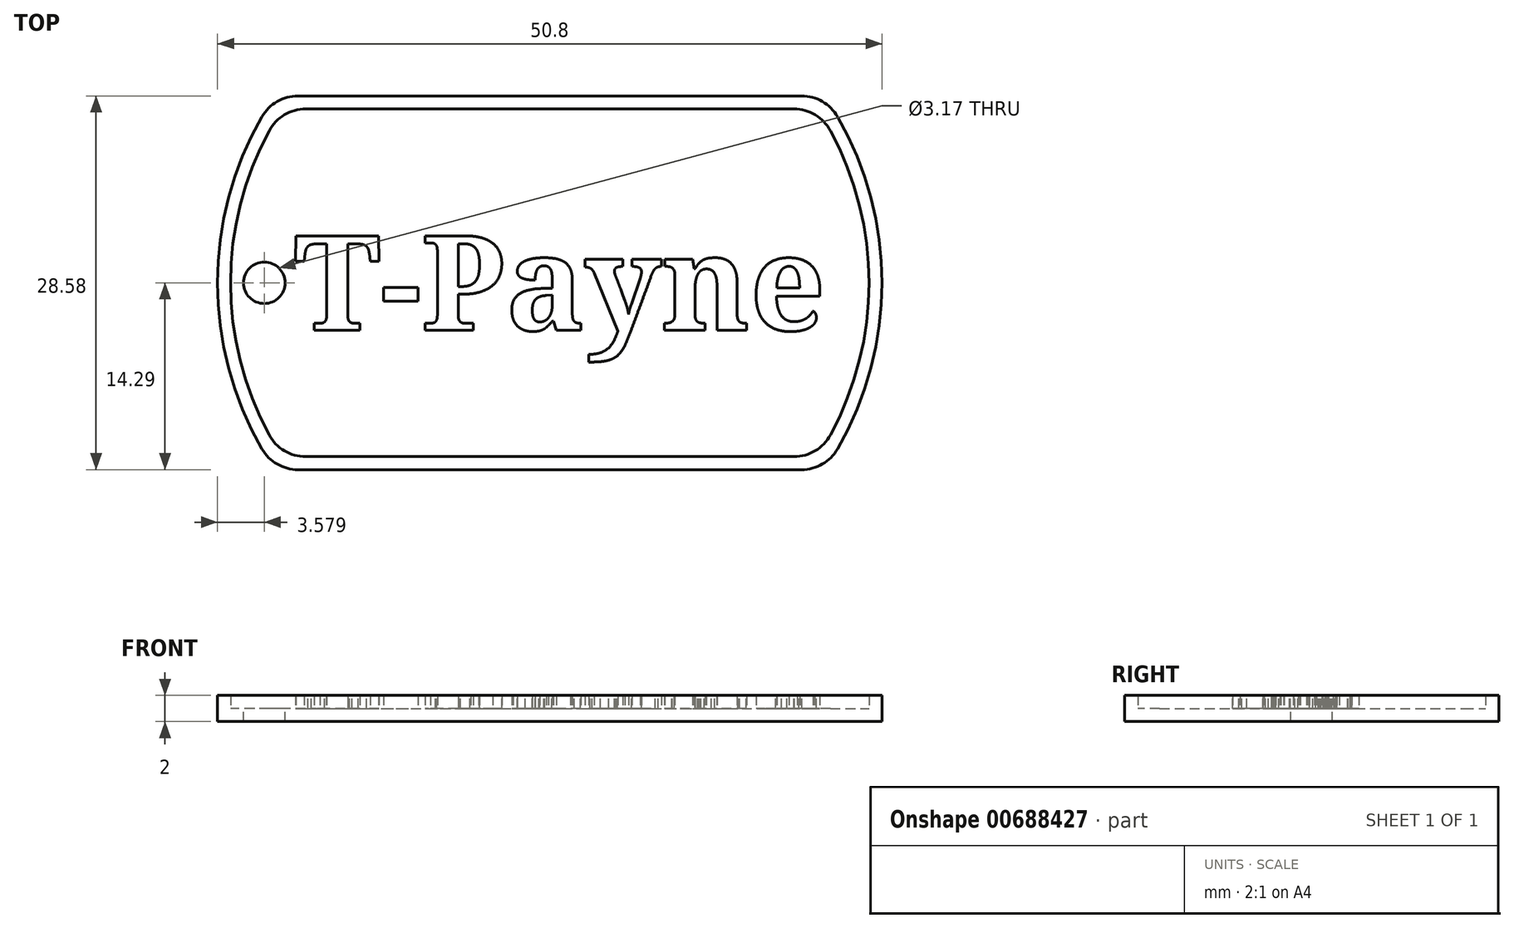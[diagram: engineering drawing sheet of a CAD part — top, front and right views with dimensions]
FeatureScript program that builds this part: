
annotation { "Feature Type Name" : "Feature", "Feature Type Description" : "" }
export const myFeature = defineFeature(function(context is Context, id is Id, definition is map)
    precondition{}
    {
        {
            var Q0;
            Q0=qCreatedBy(makeId("Top.planeOp"),FACE);
            var sketch = newSketch(context, id + "F0", { "sketchPlane" : qUnion([Q0])});
            skArc(sketch, "E0", {"start": v(-22, 12.7) * mm, "mid": v(-25.4, 0) * mm, "end": v(-22, -12.7) * mm});
            skLineSegment(sketch, "E1.top", {"start": v(-19.25, -14.29) * mm, "end": v(19.25, -14.29) * mm});
            skArc(sketch, "E2.trimOffspring", {"start": v(22, -12.7) * mm, "mid": v(25.4, 0) * mm, "end": v(22, 12.7) * mm});
            skLineSegment(sketch, "E3", {"start": v(-19.25, 14.29) * mm, "end": v(19.25, 14.29) * mm});
            skPoint(sketch, "E4.visualSharp", {"position": v(-21, 14.29) * mm});
            skArc(sketch, "E4.filletArc", {"start": v(-19.25, 14.29) * mm, "mid": v(-20.83, 13.86) * mm, "end": v(-22, 12.7) * mm});
            skPoint(sketch, "E5.visualSharp", {"position": v(21, 14.29) * mm});
            skArc(sketch, "E5.filletArc", {"start": v(22, 12.7) * mm, "mid": v(20.83, 13.86) * mm, "end": v(19.25, 14.29) * mm});
            skPoint(sketch, "E6.visualSharp", {"position": v(21, -14.29) * mm});
            skArc(sketch, "E6.filletArc", {"start": v(19.25, -14.29) * mm, "mid": v(20.83, -13.86) * mm, "end": v(22, -12.7) * mm});
            skPoint(sketch, "E7.visualSharp", {"position": v(-21, -14.29) * mm});
            skArc(sketch, "E7.filletArc", {"start": v(-22, -12.7) * mm, "mid": v(-20.83, -13.86) * mm, "end": v(-19.25, -14.29) * mm});
            skSolve(sketch);
        }
        {
            var Q0;
            Q0=makeQuery(id+"F0.imprint","IMPRINT",FACE,{"disambiguationData":[TD([[makeQuery(id+"F0.imprint","IMPRINT",EDGE,{"derivedFrom":sQuery(id+"F0.wireOp",EDGE,"E0")}),1.0]])]});
            extrude(context, id + "F1", {"entities" : qUnion([Q0]), "depth" : 1 * mm, "offsetDistance" : 25.4 * mm});
        }
        {
            var Q0;
            Q0=makeQuery(id+"F1.opExtrude","CAP_FACE",FACE,{"disambiguationData":[OSD([sQuery(id+"F0.wireOp",EDGE,"E0"),sQuery(id+"F0.wireOp",EDGE,"E1.top"),sQuery(id+"F0.wireOp",EDGE,"E2.trimOffspring"),sQuery(id+"F0.wireOp",EDGE,"E3"),sQuery(id+"F0.wireOp",EDGE,"E4.filletArc"),sQuery(id+"F0.wireOp",EDGE,"E5.filletArc"),sQuery(id+"F0.wireOp",EDGE,"E6.filletArc"),sQuery(id+"F0.wireOp",EDGE,"E7.filletArc")])],"isStart":false});
            var sketch = newSketch(context, id + "F2", { "sketchPlane" : qUnion([Q0])});
            skLineSegment(sketch, "E8.0", {"start": v(-18.66, 13.29) * mm, "end": v(18.66, 13.29) * mm});
            skArc(sketch, "E8.1", {"start": v(-21.45, 11.63) * mm, "mid": v(-24.4, 0) * mm, "end": v(-21.45, -11.63) * mm});
            skLineSegment(sketch, "E8.2", {"start": v(-18.66, -13.29) * mm, "end": v(18.66, -13.29) * mm});
            skArc(sketch, "E8.3", {"start": v(21.45, -11.63) * mm, "mid": v(24.4, 0) * mm, "end": v(21.45, 11.63) * mm});
            skPoint(sketch, "E9.visualSharp", {"position": v(-20.46, 13.29) * mm});
            skArc(sketch, "E9.filletArc", {"start": v(-18.66, 13.29) * mm, "mid": v(-20.29, 12.84) * mm, "end": v(-21.45, 11.63) * mm});
            skPoint(sketch, "E10.visualSharp", {"position": v(20.46, 13.29) * mm});
            skArc(sketch, "E10.filletArc", {"start": v(21.45, 11.63) * mm, "mid": v(20.29, 12.84) * mm, "end": v(18.66, 13.29) * mm});
            skPoint(sketch, "E11.visualSharp", {"position": v(20.46, -13.29) * mm});
            skArc(sketch, "E11.filletArc", {"start": v(18.66, -13.29) * mm, "mid": v(20.29, -12.84) * mm, "end": v(21.45, -11.63) * mm});
            skPoint(sketch, "E12.visualSharp", {"position": v(-20.46, -13.29) * mm});
            skArc(sketch, "E12.filletArc", {"start": v(-21.45, -11.63) * mm, "mid": v(-20.29, -12.84) * mm, "end": v(-18.66, -13.29) * mm});
            skLineSegment(sketch, "E13.0", {"start": v(-19.25, 14.29) * mm, "end": v(19.25, 14.29) * mm});
            skArc(sketch, "E13.1", {"start": v(-22, 12.7) * mm, "mid": v(-25.4, 0) * mm, "end": v(-22, -12.7) * mm});
            skLineSegment(sketch, "E13.2", {"start": v(-19.25, -14.29) * mm, "end": v(19.25, -14.29) * mm});
            skArc(sketch, "E13.3", {"start": v(22, -12.7) * mm, "mid": v(25.4, 0) * mm, "end": v(22, 12.7) * mm});
            skPoint(sketch, "E14.visualSharp", {"position": v(-21, -14.29) * mm});
            skArc(sketch, "E14.filletArc", {"start": v(-22, -12.7) * mm, "mid": v(-20.83, -13.86) * mm, "end": v(-19.25, -14.29) * mm});
            skPoint(sketch, "E15.visualSharp", {"position": v(21, -14.29) * mm});
            skArc(sketch, "E15.filletArc", {"start": v(19.25, -14.29) * mm, "mid": v(20.83, -13.86) * mm, "end": v(22, -12.7) * mm});
            skPoint(sketch, "E16.visualSharp", {"position": v(21, 14.29) * mm});
            skArc(sketch, "E16.filletArc", {"start": v(22, 12.7) * mm, "mid": v(20.83, 13.86) * mm, "end": v(19.25, 14.29) * mm});
            skPoint(sketch, "E17.visualSharp", {"position": v(-21, 14.29) * mm});
            skArc(sketch, "E17.filletArc", {"start": v(-19.25, 14.29) * mm, "mid": v(-20.83, 13.86) * mm, "end": v(-22, 12.7) * mm});
            skSolve(sketch);
        }
        {
            var Q0;
            Q0=makeQuery(id+"F2.imprint","IMPRINT",FACE,{"disambiguationData":[TD([[makeQuery(id+"F2.imprint","IMPRINT",EDGE,{"derivedFrom":sQuery(id+"F2.wireOp",EDGE,"E8.0")}),1.0]])]});
            extrude(context, id + "F3", {"entities" : qUnion([Q0]), "operationType" : NewBodyOperationType.ADD, "depth" : 1 * mm, "offsetDistance" : 25.4 * mm});
        }
        {
            var Q0;
            Q0=makeQuery(id+"F1.opExtrude","CAP_FACE",FACE,{"disambiguationData":[OSD([sQuery(id+"F0.wireOp",EDGE,"E0"),sQuery(id+"F0.wireOp",EDGE,"E1.top"),sQuery(id+"F0.wireOp",EDGE,"E2.trimOffspring"),sQuery(id+"F0.wireOp",EDGE,"E3"),sQuery(id+"F0.wireOp",EDGE,"E4.filletArc"),sQuery(id+"F0.wireOp",EDGE,"E5.filletArc"),sQuery(id+"F0.wireOp",EDGE,"E6.filletArc"),sQuery(id+"F0.wireOp",EDGE,"E7.filletArc")])],"isStart":false});
            var sketch = newSketch(context, id + "F4", { "sketchPlane" : qUnion([Q0])});
            skCircle(sketch, "E18", {"center": v(-21.82, 0) * mm, "radius": 1.59 * mm});
            skSolve(sketch);
        }
        {
            var Q0;
            Q0=makeQuery(id+"F4.imprint","IMPRINT",FACE,{"disambiguationData":[TD([[makeQuery(id+"F4.imprint","IMPRINT",EDGE,{"derivedFrom":sQuery(id+"F4.wireOp",EDGE,"E18")}),1.0]])]});
            extrude(context, id + "F5", {"entities" : qUnion([Q0]), "operationType" : NewBodyOperationType.REMOVE, "oppositeDirection" : true, "depth" : 1 * mm, "offsetDistance" : 25.4 * mm});
        }
        {
            var Q0;
            Q0=makeQuery(id+"F2.imprint","IMPRINT",FACE,{"disambiguationData":[TD([[makeQuery(id+"F2.imprint","IMPRINT",EDGE,{"derivedFrom":sQuery(id+"F2.wireOp",EDGE,"E8.0")}),-1.0]])]});
            var sketch = newSketch(context, id + "F6", { "sketchPlane" : qUnion([Q0])});
            skText(sketch, "E19", { "text": "T-Payne", "fontName": "NotoSerif-Bold.ttf"});
            const initialGuessF6  = {"E19": [-0.01955, -0.00363, 1, 0, 0.00728]};
            skSetInitialGuess(sketch, initialGuessF6);
            skSolve(sketch);
        }
        {
            var Q0;
            Q0 = qSketchRegion(id + "F6", true);
            extrude(context, id + "F7", {"entities" : qUnion([Q0]), "operationType" : NewBodyOperationType.ADD, "depth" : 1 * mm, "offsetDistance" : 25.4 * mm});
        }
    });
